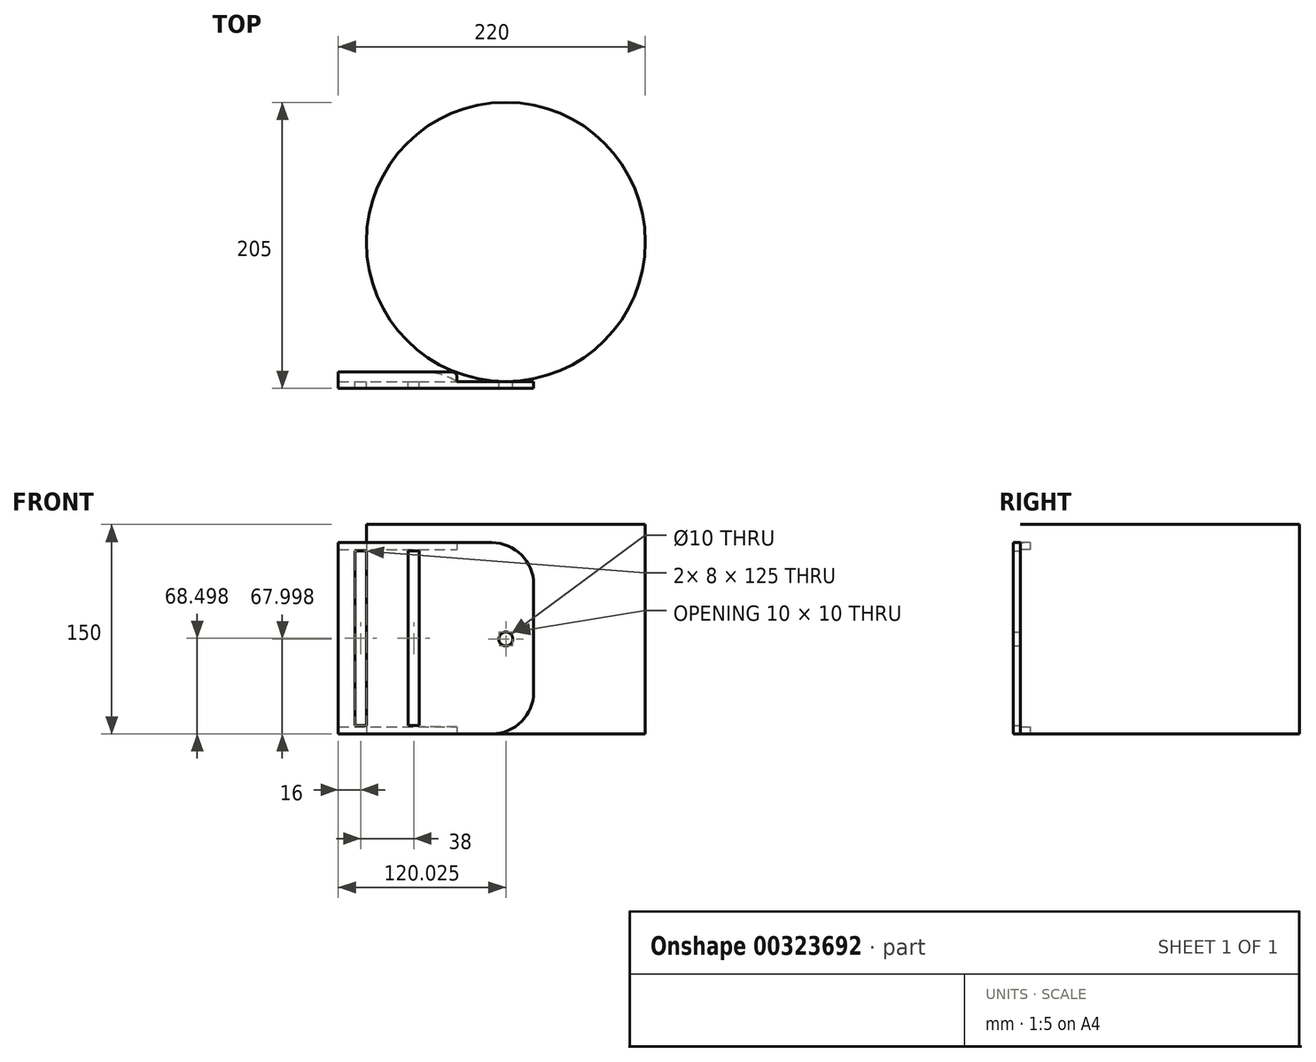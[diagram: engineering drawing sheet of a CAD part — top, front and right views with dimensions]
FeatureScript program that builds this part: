
annotation { "Feature Type Name" : "Feature", "Feature Type Description" : "" }
export const myFeature = defineFeature(function(context is Context, id is Id, definition is map)
    precondition{}
    {
        {
            var Q0;
            Q0=qCreatedBy(makeId("Front.planeOp"),FACE);
            var sketch = newSketch(context, id + "F0", { "sketchPlane" : qUnion([Q0])});
            skLineSegment(sketch, "E0.bottom", {"start": v(0, 141.42) * mm, "end": v(0, 141.42) * mm});
            skLineSegment(sketch, "E0.top", {"start": v(0, -141.42) * mm, "end": v(0, -141.42) * mm});
            skPoint(sketch, "E0.middle", {"position": v(0, 0) * mm});
            skLineSegment(sketch, "E1.bottom", {"start": v(0, 0) * mm, "end": v(-140, 0) * mm});
            skLineSegment(sketch, "E1.top", {"start": v(0, 137) * mm, "end": v(-140, 137) * mm});
            skLineSegment(sketch, "E1.left", {"start": v(0, 0) * mm, "end": v(0, 137) * mm});
            skLineSegment(sketch, "E1.right", {"start": v(-140, 0) * mm, "end": v(-140, 137) * mm});
            skLineSegment(sketch, "E2.bottom", {"start": v(-128, 131) * mm, "end": v(-120, 131) * mm});
            skLineSegment(sketch, "E2.top", {"start": v(-128, 6) * mm, "end": v(-120, 6) * mm});
            skLineSegment(sketch, "E2.left", {"start": v(-128, 131) * mm, "end": v(-128, 6) * mm});
            skLineSegment(sketch, "E2.right", {"start": v(-120, 131) * mm, "end": v(-120, 6) * mm});
            skPoint(sketch, "E3", {"position": v(-124, 6) * mm});
            skPoint(sketch, "E4", {"position": v(-124.16, 0) * mm});
            skPoint(sketch, "E5", {"position": v(-97, 6) * mm});
            skPoint(sketch, "E6", {"position": v(-97, 0) * mm});
            skPoint(sketch, "E7", {"position": v(-128, 131) * mm});
            skPoint(sketch, "E8", {"position": v(-140, 131) * mm});
            skLineSegment(sketch, "E9.bottom", {"start": v(-90, 131) * mm, "end": v(-82, 131) * mm});
            skLineSegment(sketch, "E9.top", {"start": v(-90, 6) * mm, "end": v(-82, 6) * mm});
            skLineSegment(sketch, "E9.left", {"start": v(-90, 131) * mm, "end": v(-90, 6) * mm});
            skLineSegment(sketch, "E9.right", {"start": v(-82, 131) * mm, "end": v(-82, 6) * mm});
            skPoint(sketch, "E10", {"position": v(-82, 131) * mm});
            skPoint(sketch, "E11", {"position": v(-82, 6) * mm});
            skPoint(sketch, "E12", {"position": v(-90, 131) * mm});
            skPoint(sketch, "E13", {"position": v(-120, 131) * mm});
            skPoint(sketch, "E14", {"position": v(-75.2, 137) * mm});
            skPoint(sketch, "E15", {"position": v(0, 68.5) * mm});
            skCircle(sketch, "E16", {"center": v(-19.97, 68) * mm, "radius": 5 * mm});
            skPoint(sketch, "E17", {"position": v(-15, 68.5) * mm});
            skPoint(sketch, "E17.positionSnap0", {"position": v(-82, 68.5) * mm});
            skSolve(sketch);
        }
        {
            var Q0;
            Q0 = qSketchRegion(id + "F0", true);
            extrude(context, id + "F1", {"entities" : qUnion([Q0]), "depth" : 5 * mm});
        }
        {
            var Q0;
            Q0=makeQuery(id+"F1.opExtrude","SWEPT_EDGE",EDGE,{"disambiguationData":[OSD([sQuery(id+"F0.wireOp",EDGE,"E1.top"),sQuery(id+"F0.wireOp",EDGE,"E1.left")])]});
            fillet(context, id + "F2", {"entities" : qUnion([Q0]), "radius" : 30 * mm, "tangentPropagation" : true, "allowEdgeOverflow" : false});
        }
        {
            var Q0;
            Q0=makeQuery(id+"F1.opExtrude","SWEPT_EDGE",EDGE,{"disambiguationData":[OSD([sQuery(id+"F0.wireOp",EDGE,"E1.bottom"),sQuery(id+"F0.wireOp",EDGE,"E1.left")])]});
            fillet(context, id + "F3", {"entities" : qUnion([Q0]), "radius" : 30 * mm, "tangentPropagation" : true, "allowEdgeOverflow" : false});
        }
        {
            var Q0;
            Q0=qCreatedBy(makeId("Top.planeOp"),FACE);
            var sketch = newSketch(context, id + "F4", { "sketchPlane" : qUnion([Q0])});
            skLineSegment(sketch, "E18.bottom", {"start": v(-140, 0) * mm, "end": v(-55, 0) * mm});
            skLineSegment(sketch, "E18.top", {"start": v(-140, 7) * mm, "end": v(-55, 7) * mm});
            skLineSegment(sketch, "E18.left", {"start": v(-140, 0) * mm, "end": v(-140, 7) * mm});
            skLineSegment(sketch, "E18.right", {"start": v(-55, 0) * mm, "end": v(-55, 7) * mm});
            skSolve(sketch);
        }
        {
            var Q0;
            Q0 = qSketchRegion(id + "F4", true);
            extrude(context, id + "F5", {"entities" : qUnion([Q0]), "operationType" : NewBodyOperationType.ADD, "depth" : 5 * mm});
        }
        {
            var Q0;
            Q0=makeQuery(id+"F5.opExtrude","SWEPT_EDGE",EDGE,{"disambiguationData":[OSD([sQuery(id+"F4.wireOp",EDGE,"E18.top"),sQuery(id+"F4.wireOp",EDGE,"E18.right")])]});
            fillet(context, id + "F6", {"entities" : qUnion([Q0]), "radius" : 50 * mm, "tangentPropagation" : true, "allowEdgeOverflow" : false});
        }
        {
            var Q0;
            Q0=qCreatedBy(makeId("Front.planeOp"),FACE);
            var sketch = newSketch(context, id + "F7", { "sketchPlane" : qUnion([Q0])});
            skLineSegment(sketch, "E19.bottom", {"start": v(-140, 137) * mm, "end": v(-55, 137) * mm});
            skLineSegment(sketch, "E19.top", {"start": v(-140, 132) * mm, "end": v(-55, 132) * mm});
            skLineSegment(sketch, "E19.left", {"start": v(-140, 137) * mm, "end": v(-140, 132) * mm});
            skLineSegment(sketch, "E19.right", {"start": v(-55, 137) * mm, "end": v(-55, 132) * mm});
            skPoint(sketch, "E20", {"position": v(-140, 132) * mm});
            skSolve(sketch);
        }
        {
            var Q0;
            Q0 = qSketchRegion(id + "F7", true);
            extrude(context, id + "F8", {"entities" : qUnion([Q0]), "operationType" : NewBodyOperationType.ADD, "oppositeDirection" : true, "depth" : 7 * mm});
        }
        {
            var Q0;
            Q0=makeQuery(id+"F8.opExtrude","CAP_EDGE",EDGE,{"disambiguationData":[OSD([sQuery(id+"F7.wireOp",EDGE,"E19.right")])],"isStart":false});
            fillet(context, id + "F9", {"entities" : qUnion([Q0]), "radius" : 4 * mm, "tangentPropagation" : true, "allowEdgeOverflow" : false});
        }
        {
            var Q0;
            Q0=qCreatedBy(makeId("Top.planeOp"),FACE);
            var sketch = newSketch(context, id + "F10", { "sketchPlane" : qUnion([Q0])});
            skCircle(sketch, "E21", {"center": v(-20, 100) * mm, "radius": 100 * mm});
            skPoint(sketch, "E22", {"position": v(38.58, 181.05) * mm});
            skPoint(sketch, "E23", {"position": v(-19.65, -100) * mm});
            skSolve(sketch);
        }
        {
            var Q0;
            Q0 = qSketchRegion(id + "F10", true);
            extrude(context, id + "F11", {"entities" : qUnion([Q0]), "operationType" : NewBodyOperationType.ADD, "depth" : 150 * mm});
        }
    });
